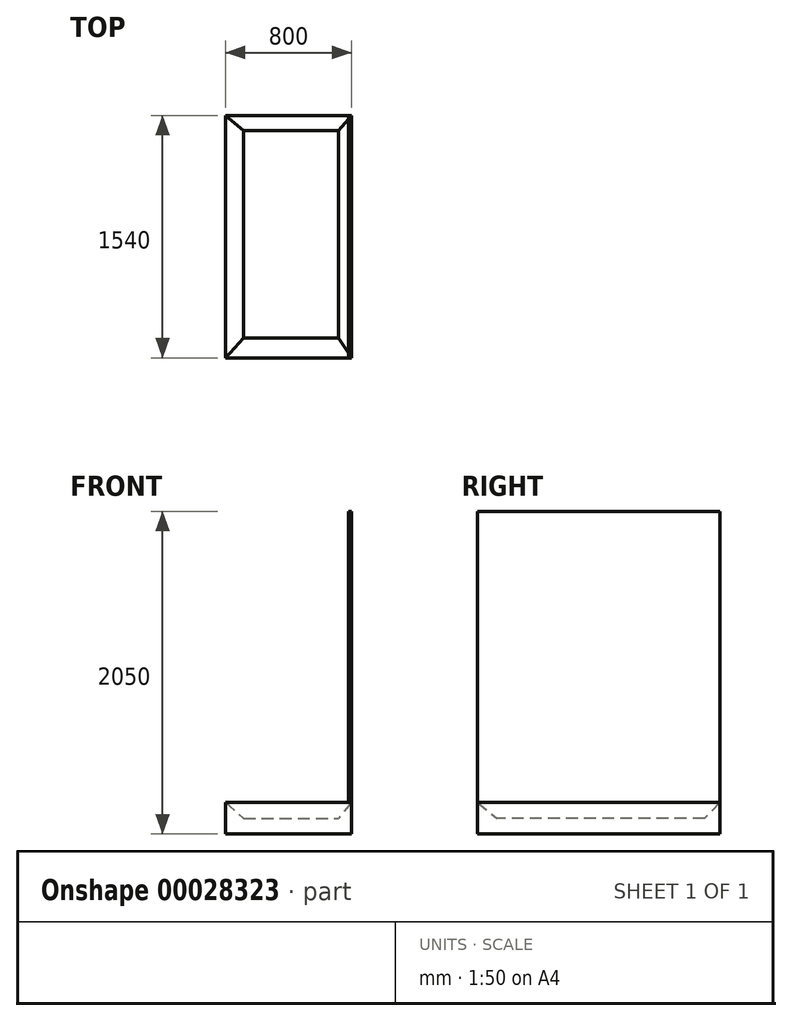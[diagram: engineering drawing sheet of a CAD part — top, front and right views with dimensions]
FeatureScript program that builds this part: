
annotation { "Feature Type Name" : "Feature", "Feature Type Description" : "" }
export const myFeature = defineFeature(function(context is Context, id is Id, definition is map)
    precondition{}
    {
        {
            var Q0;
            Q0=qCreatedBy(makeId("Top.planeOp"),FACE);
            var sketch = newSketch(context, id + "F0", { "sketchPlane" : qUnion([Q0])});
            skLineSegment(sketch, "E0.bottom", {"start": v(-347.96, 770) * mm, "end": v(452.04, 770) * mm});
            skLineSegment(sketch, "E0.top", {"start": v(-347.96, -770) * mm, "end": v(452.04, -770) * mm});
            skLineSegment(sketch, "E0.left", {"start": v(-347.96, 770) * mm, "end": v(-347.96, -770) * mm});
            skLineSegment(sketch, "E0.right", {"start": v(452.04, 770) * mm, "end": v(452.04, -770) * mm});
            skSolve(sketch);
        }
        {
            var Q0;
            Q0=makeQuery(id+"F0.imprint","IMPRINT",FACE,{"disambiguationData":[TD([[makeQuery(id+"F0.imprint","IMPRINT",EDGE,{"derivedFrom":sQuery(id+"F0.wireOp",EDGE,"E0.bottom")}),-1.0]])]});
            extrude(context, id + "F1", {"entities" : qUnion([Q0]), "depth" : 200 * mm});
        }
        {
            var Q0;
            Q0=makeQuery(id+"F1.opExtrude","CAP_FACE",FACE,{"disambiguationData":[OSD([sQuery(id+"F0.wireOp",EDGE,"E0.bottom"),sQuery(id+"F0.wireOp",EDGE,"E0.top"),sQuery(id+"F0.wireOp",EDGE,"E0.left"),sQuery(id+"F0.wireOp",EDGE,"E0.right")])],"isStart":false});
            var sketch = newSketch(context, id + "F2", { "sketchPlane" : qUnion([Q0])});
            skLineSegment(sketch, "E1.bottom", {"start": v(452.04, 770) * mm, "end": v(432.04, 770) * mm});
            skLineSegment(sketch, "E1.top", {"start": v(452.04, -770) * mm, "end": v(432.04, -770) * mm});
            skLineSegment(sketch, "E1.left", {"start": v(452.04, 770) * mm, "end": v(452.04, -770) * mm});
            skLineSegment(sketch, "E1.right", {"start": v(432.04, 770) * mm, "end": v(432.04, -770) * mm});
            skSolve(sketch);
        }
        {
            var Q0;
            Q0 = qSketchRegion(id + "F2", true);
            extrude(context, id + "F3", {"entities" : qUnion([Q0]), "depth" : 1850 * mm});
        }
        {
            var Q0;
            Q0=makeQuery(id+"F1.opExtrude","CAP_FACE",FACE,{"disambiguationData":[OSD([sQuery(id+"F0.wireOp",EDGE,"E0.bottom"),sQuery(id+"F0.wireOp",EDGE,"E0.top"),sQuery(id+"F0.wireOp",EDGE,"E0.left"),sQuery(id+"F0.wireOp",EDGE,"E0.right")])],"isStart":false});
            cPlane(context, id + "F4", {"entities" : qUnion([Q0]), "cplaneType" : CPlaneType.OFFSET, "offset" : 100 * mm, "oppositeDirection" : true, "width" : 150 * mm, "height" : 150 * mm});
        }
        {
            var Q0;
            Q0=qCreatedBy(id+"F4.planeOp",FACE);
            var sketch = newSketch(context, id + "F5", { "sketchPlane" : qUnion([Q0])});
            skLineSegment(sketch, "E2.bottom", {"start": v(-234.08, 672.37) * mm, "end": v(368.33, 672.37) * mm});
            skLineSegment(sketch, "E2.top", {"start": v(-234.08, -645.53) * mm, "end": v(368.33, -645.53) * mm});
            skLineSegment(sketch, "E2.left", {"start": v(-234.08, 672.37) * mm, "end": v(-234.08, -645.53) * mm});
            skLineSegment(sketch, "E2.right", {"start": v(368.33, 672.37) * mm, "end": v(368.33, -645.53) * mm});
            skPoint(sketch, "E3.0", {"position": v(-347.96, 770) * mm});
            skPoint(sketch, "E4.0", {"position": v(452.04, -770) * mm});
            skSolve(sketch);
        }
        {
            var Q1;
            Q1=makeQuery(id+"F1.opExtrude","CAP_FACE",FACE,{"disambiguationData":[OSD([sQuery(id+"F0.wireOp",EDGE,"E0.bottom"),sQuery(id+"F0.wireOp",EDGE,"E0.top"),sQuery(id+"F0.wireOp",EDGE,"E0.left"),sQuery(id+"F0.wireOp",EDGE,"E0.right")])],"isStart":false});
            var Q2;
            Q2 = qSketchRegion(id + "F5", true);
            loft(context, id + "F6", {"operationType" : NewBodyOperationType.REMOVE, "sheetProfilesArray" : [{ "sheetProfileEntities" : qUnion([Q1]) }, { "sheetProfileEntities" : qUnion([Q2]) }]});
        }
    });
